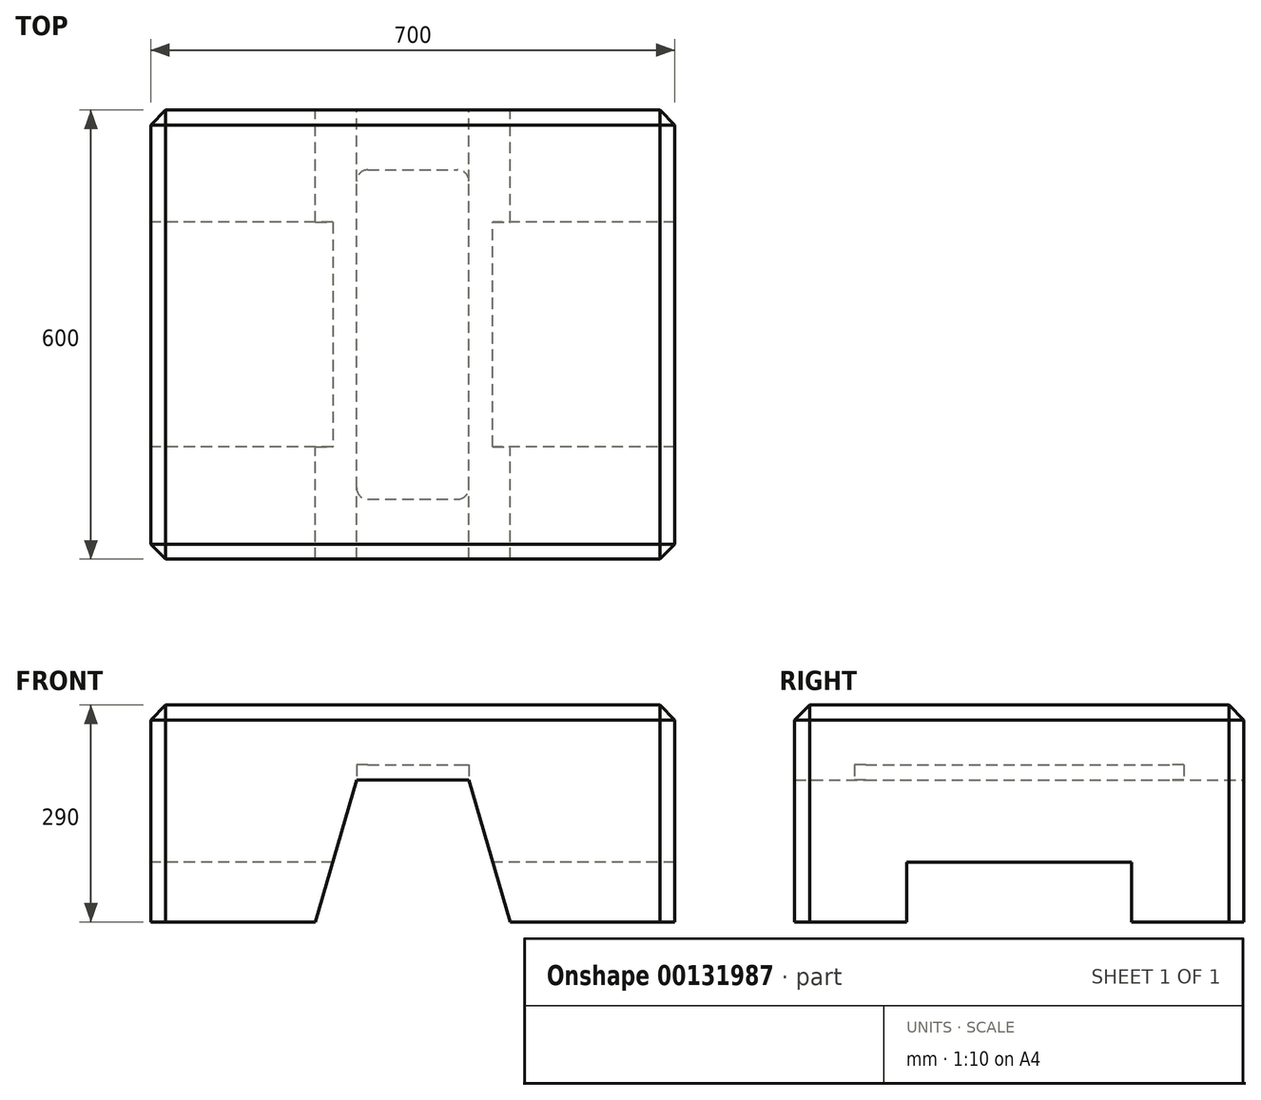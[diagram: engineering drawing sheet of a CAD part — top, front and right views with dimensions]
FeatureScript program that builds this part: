
annotation { "Feature Type Name" : "Feature", "Feature Type Description" : "" }
export const myFeature = defineFeature(function(context is Context, id is Id, definition is map)
    precondition{}
    {
        {
            var Q0;
            Q0=qCreatedBy(makeId("Front.planeOp"),FACE);
            var sketch = newSketch(context, id + "F0", { "sketchPlane" : qUnion([Q0])});
            skLineSegment(sketch, "E0.bottom", {"start": v(0, 0) * mm, "end": v(-220, 0) * mm});
            skLineSegment(sketch, "E0.top", {"start": v(0, 290) * mm, "end": v(-700, 290) * mm});
            skLineSegment(sketch, "E0.left", {"start": v(0, 0) * mm, "end": v(0, 290) * mm});
            skLineSegment(sketch, "E0.right", {"start": v(-700, 0) * mm, "end": v(-700, 290) * mm});
            skLineSegment(sketch, "E1", {"start": v(-480, 0) * mm, "end": v(-425, 190) * mm});
            skLineSegment(sketch, "E2", {"start": v(-425, 190) * mm, "end": v(-275, 190) * mm});
            skLineSegment(sketch, "E3", {"start": v(-275, 190) * mm, "end": v(-220, 0) * mm});
            skLineSegment(sketch, "E4.trimOffspring", {"start": v(-480, 0) * mm, "end": v(-700, 0) * mm});
            skSolve(sketch);
        }
        {
            var Q0;
            Q0=makeQuery(id+"F0.imprint","IMPRINT",FACE,{"disambiguationData":[TD([[makeQuery(id+"F0.imprint","IMPRINT",EDGE,{"derivedFrom":sQuery(id+"F0.wireOp",EDGE,"E0.bottom")}),-1.0]])]});
            extrude(context, id + "F1", {"entities" : qUnion([Q0]), "depth" : 600 * mm});
        }
        {
            var Q0;
            Q0=makeQuery(id+"F1.opExtrude","SWEPT_FACE",FACE,{"disambiguationData":[OSD([sQuery(id+"F0.wireOp",EDGE,"E0.bottom")])]});
            var sketch = newSketch(context, id + "F2", { "sketchPlane" : qUnion([Q0])});
            skLineSegment(sketch, "E5.bottom", {"start": v(30, 150) * mm, "end": v(-730, 150) * mm});
            skLineSegment(sketch, "E5.top", {"start": v(30, 450) * mm, "end": v(-730, 450) * mm});
            skLineSegment(sketch, "E5.left", {"start": v(30, 150) * mm, "end": v(30, 450) * mm});
            skLineSegment(sketch, "E5.right", {"start": v(-730, 150) * mm, "end": v(-730, 450) * mm});
            skSolve(sketch);
        }
        {
            var Q0;
            Q0 = qSketchRegion(id + "F2", true);
            extrude(context, id + "F3", {"entities" : qUnion([Q0]), "operationType" : NewBodyOperationType.REMOVE, "oppositeDirection" : true, "depth" : 80 * mm});
        }
        {
            var Q0;
            Q0=makeQuery(id+"F1.opExtrude","SWEPT_FACE",FACE,{"disambiguationData":[OSD([sQuery(id+"F0.wireOp",EDGE,"E2")])]});
            var sketch = newSketch(context, id + "F4", { "sketchPlane" : qUnion([Q0])});
            skLineSegment(sketch, "E6.bottom", {"start": v(-425, 80) * mm, "end": v(-275, 80) * mm});
            skLineSegment(sketch, "E6.top", {"start": v(-425, 520) * mm, "end": v(-275, 520) * mm});
            skLineSegment(sketch, "E6.left", {"start": v(-425, 80) * mm, "end": v(-425, 520) * mm});
            skLineSegment(sketch, "E6.right", {"start": v(-275, 80) * mm, "end": v(-275, 520) * mm});
            skSolve(sketch);
        }
        {
            var Q0;
            Q0 = qSketchRegion(id + "F4", true);
            extrude(context, id + "F5", {"entities" : qUnion([Q0]), "operationType" : NewBodyOperationType.REMOVE, "oppositeDirection" : true, "depth" : 20 * mm});
        }
        {
            var Q0;
            Q0=makeQuery(id+"F1.opExtrude","CAP_EDGE",EDGE,{"disambiguationData":[OSD([sQuery(id+"F0.wireOp",EDGE,"E0.right")])],"isStart":true});
            var Q1;
            Q1=makeQuery(id+"F1.opExtrude","SWEPT_EDGE",EDGE,{"disambiguationData":[OSD([sQuery(id+"F0.wireOp",EDGE,"E0.top"),sQuery(id+"F0.wireOp",EDGE,"E0.right")])]});
            var Q2;
            Q2=makeQuery(id+"F1.opExtrude","CAP_EDGE",EDGE,{"disambiguationData":[OSD([sQuery(id+"F0.wireOp",EDGE,"E0.top")])],"isStart":true});
            var Q3;
            Q3=makeQuery(id+"F1.opExtrude","SWEPT_EDGE",EDGE,{"disambiguationData":[OSD([sQuery(id+"F0.wireOp",EDGE,"E0.top"),sQuery(id+"F0.wireOp",EDGE,"E0.left")])]});
            var Q4;
            Q4=makeQuery(id+"F1.opExtrude","CAP_EDGE",EDGE,{"disambiguationData":[OSD([sQuery(id+"F0.wireOp",EDGE,"E0.top")])],"isStart":false});
            var Q5;
            Q5=makeQuery(id+"F1.opExtrude","CAP_EDGE",EDGE,{"disambiguationData":[OSD([sQuery(id+"F0.wireOp",EDGE,"E0.right")])],"isStart":false});
            var Q6;
            Q6=makeQuery(id+"F1.opExtrude","CAP_EDGE",EDGE,{"disambiguationData":[OSD([sQuery(id+"F0.wireOp",EDGE,"E0.left")])],"isStart":false});
            var Q7;
            Q7=makeQuery(id+"F1.opExtrude","CAP_EDGE",EDGE,{"disambiguationData":[OSD([sQuery(id+"F0.wireOp",EDGE,"E0.left")])],"isStart":true});
            chamfer(context, id + "F6", {"entities" : qUnion([Q0, Q1, Q2, Q3, Q4, Q5, Q6, Q7]), "width" : 20 * mm, "tangentPropagation" : true});
        }
        {
            var Q0;
            Q0=makeQuery(id+"F5.boolean.opBoolean","COPY",EDGE,{"derivedFrom":makeQuery(id+"F5.opExtrude","SWEPT_EDGE",EDGE,{"disambiguationData":[OSD([sQuery(id+"F0.wireOp",EDGE,"E1"),sQuery(id+"F0.wireOp",EDGE,"E2"),sQuery(id+"F4.wireOp",EDGE,"E6.top"),sQuery(id+"F4.wireOp",EDGE,"E6.left")])]})});
            var Q1;
            Q1=makeQuery(id+"F5.boolean.opBoolean","COPY",EDGE,{"derivedFrom":makeQuery(id+"F5.opExtrude","SWEPT_EDGE",EDGE,{"disambiguationData":[OSD([sQuery(id+"F0.wireOp",EDGE,"E2"),sQuery(id+"F0.wireOp",EDGE,"E3"),sQuery(id+"F4.wireOp",EDGE,"E6.top"),sQuery(id+"F4.wireOp",EDGE,"E6.right")])]})});
            var Q2;
            Q2=makeQuery(id+"F5.boolean.opBoolean","COPY",EDGE,{"derivedFrom":makeQuery(id+"F5.opExtrude","SWEPT_EDGE",EDGE,{"disambiguationData":[OSD([sQuery(id+"F0.wireOp",EDGE,"E1"),sQuery(id+"F0.wireOp",EDGE,"E2"),sQuery(id+"F4.wireOp",EDGE,"E6.bottom"),sQuery(id+"F4.wireOp",EDGE,"E6.left")])]})});
            var Q3;
            Q3=makeQuery(id+"F5.boolean.opBoolean","COPY",EDGE,{"derivedFrom":makeQuery(id+"F5.opExtrude","SWEPT_EDGE",EDGE,{"disambiguationData":[OSD([sQuery(id+"F0.wireOp",EDGE,"E2"),sQuery(id+"F0.wireOp",EDGE,"E3"),sQuery(id+"F4.wireOp",EDGE,"E6.bottom"),sQuery(id+"F4.wireOp",EDGE,"E6.right")])]})});
            fillet(context, id + "F7", {"entities" : qUnion([Q0, Q1, Q2, Q3]), "radius" : 15 * mm, "tangentPropagation" : true, "allowEdgeOverflow" : false});
        }
    });
